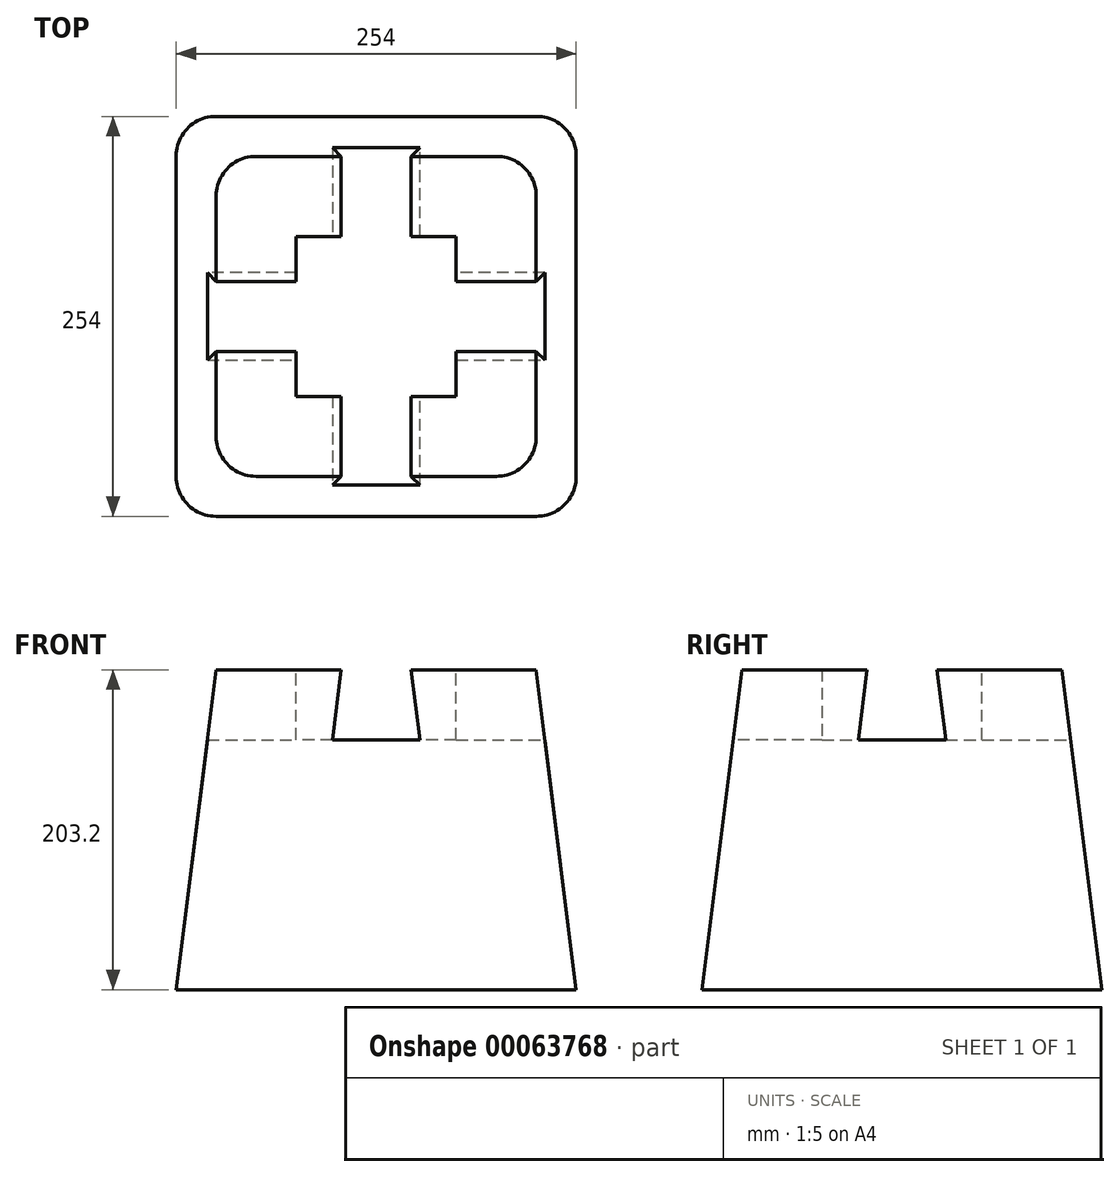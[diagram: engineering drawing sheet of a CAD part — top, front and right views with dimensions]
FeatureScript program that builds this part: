
annotation { "Feature Type Name" : "Feature", "Feature Type Description" : "" }
export const myFeature = defineFeature(function(context is Context, id is Id, definition is map)
    precondition{}
    {
        {
            var Q0;
            Q0=qCreatedBy(makeId("Top.planeOp"),FACE);
            var sketch = newSketch(context, id + "F0", { "sketchPlane" : qUnion([Q0])});
            skLineSegment(sketch, "E0.bottom", {"start": v(-127.47, 138) * mm, "end": v(126.53, 138) * mm});
            skLineSegment(sketch, "E0.top", {"start": v(-127.47, -116) * mm, "end": v(126.53, -116) * mm});
            skLineSegment(sketch, "E0.left", {"start": v(-127.47, 138) * mm, "end": v(-127.47, -116) * mm});
            skLineSegment(sketch, "E0.right", {"start": v(126.53, 138) * mm, "end": v(126.53, -116) * mm});
            skSolve(sketch);
        }
        {
            var Q0;
            Q0 = qSketchRegion(id + "F0", true);
            extrude(context, id + "F1", {"entities" : qUnion([Q0]), "depth" : 203.2 * mm, "hasDraft" : true, "draftAngle" : 7.12 * degree, "draftPullDirection" : true});
        }
        {
            var Q0;
            Q0=makeQuery(id+"F1.opExtrude","SWEPT_EDGE",EDGE,{"disambiguationData":[OSD([sQuery(id+"F0.wireOp",EDGE,"E0.top"),sQuery(id+"F0.wireOp",EDGE,"E0.left")])]});
            var Q1;
            Q1=makeQuery(id+"F1.opExtrude","SWEPT_EDGE",EDGE,{"disambiguationData":[OSD([sQuery(id+"F0.wireOp",EDGE,"E0.top"),sQuery(id+"F0.wireOp",EDGE,"E0.right")])]});
            var Q2;
            Q2=makeQuery(id+"F1.opExtrude","SWEPT_EDGE",EDGE,{"disambiguationData":[OSD([sQuery(id+"F0.wireOp",EDGE,"E0.bottom"),sQuery(id+"F0.wireOp",EDGE,"E0.right")])]});
            var Q3;
            Q3=makeQuery(id+"F1.opExtrude","SWEPT_EDGE",EDGE,{"disambiguationData":[OSD([sQuery(id+"F0.wireOp",EDGE,"E0.bottom"),sQuery(id+"F0.wireOp",EDGE,"E0.left")])]});
            fillet(context, id + "F2", {"entities" : qUnion([Q0, Q1, Q2, Q3]), "radius" : 25.4 * mm, "tangentPropagation" : true, "allowEdgeOverflow" : false});
        }
        {
            var Q0;
            Q0=makeQuery(id+"F1.opExtrude","CAP_FACE",FACE,{"disambiguationData":[OSD([sQuery(id+"F0.wireOp",EDGE,"E0.bottom"),sQuery(id+"F0.wireOp",EDGE,"E0.top"),sQuery(id+"F0.wireOp",EDGE,"E0.left"),sQuery(id+"F0.wireOp",EDGE,"E0.right")])],"isStart":false});
            var sketch = newSketch(context, id + "F3", { "sketchPlane" : qUnion([Q0])});
            skLineSegment(sketch, "E1.0", {"start": v(-102.07, 33.23) * mm, "end": v(-102.07, -11.22) * mm});
            skLineSegment(sketch, "E2.0", {"start": v(-22.7, 112.6) * mm, "end": v(21.76, 112.6) * mm});
            skLineSegment(sketch, "E3.0", {"start": v(-22.7, -90.6) * mm, "end": v(21.76, -90.6) * mm});
            skLineSegment(sketch, "E4.0", {"start": v(101.13, 33.23) * mm, "end": v(101.13, -11.22) * mm});
            skLineSegment(sketch, "E5.bottom", {"start": v(-102.07, -11.22) * mm, "end": v(-22.7, -11.22) * mm});
            skLineSegment(sketch, "E5.top", {"start": v(-102.07, 33.23) * mm, "end": v(-22.7, 33.23) * mm});
            skLineSegment(sketch, "E5.left", {"start": v(-102.07, -11.22) * mm, "end": v(-102.07, 33.23) * mm});
            skLineSegment(sketch, "E5.right", {"start": v(101.13, -11.22) * mm, "end": v(101.13, 33.23) * mm});
            skLineSegment(sketch, "E6.left", {"start": v(-22.7, -90.6) * mm, "end": v(-22.7, -11.22) * mm});
            skLineSegment(sketch, "E6.right", {"start": v(21.76, -90.6) * mm, "end": v(21.76, -11.22) * mm});
            skLineSegment(sketch, "E7.trimOffspring", {"start": v(-22.7, 33.23) * mm, "end": v(-22.7, 112.6) * mm});
            skLineSegment(sketch, "E8.trimOffspring", {"start": v(21.76, 33.23) * mm, "end": v(101.13, 33.23) * mm});
            skLineSegment(sketch, "E9.trimOffspring", {"start": v(21.76, 33.23) * mm, "end": v(21.76, 112.6) * mm});
            skLineSegment(sketch, "E10.trimOffspring", {"start": v(21.76, -11.22) * mm, "end": v(101.13, -11.22) * mm});
            skPoint(sketch, "E11.orphan", {"position": v(101.13, -65.4) * mm});
            skPoint(sketch, "E12.orphan", {"position": v(101.13, 87.4) * mm});
            skPoint(sketch, "E13.orphan", {"position": v(75.93, 112.6) * mm});
            skPoint(sketch, "E14.orphan", {"position": v(-76.86, 112.6) * mm});
            skPoint(sketch, "E15.orphan", {"position": v(-102.07, 87.4) * mm});
            skPoint(sketch, "E16.orphan", {"position": v(-102.07, -65.4) * mm});
            skPoint(sketch, "E17.orphan", {"position": v(-76.86, -90.6) * mm});
            skPoint(sketch, "E18.orphan", {"position": v(75.93, -90.6) * mm});
            skSolve(sketch);
        }
        {
            var Q0;
            Q0 = qSketchRegion(id + "F3", true);
            extrude(context, id + "F4", {"entities" : qUnion([Q0]), "operationType" : NewBodyOperationType.REMOVE, "oppositeDirection" : true, "depth" : 44.45 * mm, "hasDraft" : true, "draftAngle" : 7.12 * degree});
        }
        {
            var Q0;
            {var subQ0=sQuery(id+"F0.wireOp",EDGE,"E0.left");var subQ1=sQuery(id+"F0.wireOp",EDGE,"E0.top");Q0=makeQuery(id+"F4.boolean.opBoolean","SPLIT",FACE,{"disambiguationData":[TD([makeQuery(id+"F4.opExtrude","SWEPT_FACE",FACE,{"disambiguationData":[OSD([sQuery(id+"F3.wireOp",EDGE,"E5.bottom")])]})])],"derivedFrom":makeQuery(id+"F1.opExtrude","CAP_FACE",FACE,{"disambiguationData":[OSD([sQuery(id+"F0.wireOp",EDGE,"E0.bottom"),subQ1,subQ0,sQuery(id+"F0.wireOp",EDGE,"E0.right")])],"isStart":false})});}
            var sketch = newSketch(context, id + "F5", { "sketchPlane" : qUnion([Q0])});
            skLineSegment(sketch, "E19.bottom", {"start": v(50.33, -39.8) * mm, "end": v(-51.27, -39.8) * mm});
            skLineSegment(sketch, "E19.top", {"start": v(50.33, 61.8) * mm, "end": v(-51.27, 61.8) * mm});
            skLineSegment(sketch, "E19.left", {"start": v(50.33, -39.8) * mm, "end": v(50.33, 61.8) * mm});
            skLineSegment(sketch, "E19.right", {"start": v(-51.27, -39.8) * mm, "end": v(-51.27, 61.8) * mm});
            skPoint(sketch, "E20.0.end.orphan", {"position": v(75.93, -90.6) * mm});
            skPoint(sketch, "E20.0.start.orphan", {"position": v(21.76, -90.6) * mm});
            skPoint(sketch, "E21.0.end.orphan", {"position": v(101.13, -65.4) * mm});
            skPoint(sketch, "E21.0.start.orphan", {"position": v(101.13, -11.22) * mm});
            skSolve(sketch);
        }
        {
            var Q0;
            Q0 = qSketchRegion(id + "F5", true);
            extrude(context, id + "F6", {"entities" : qUnion([Q0]), "operationType" : NewBodyOperationType.REMOVE, "oppositeDirection" : true, "depth" : 44.45 * mm});
        }
    });
